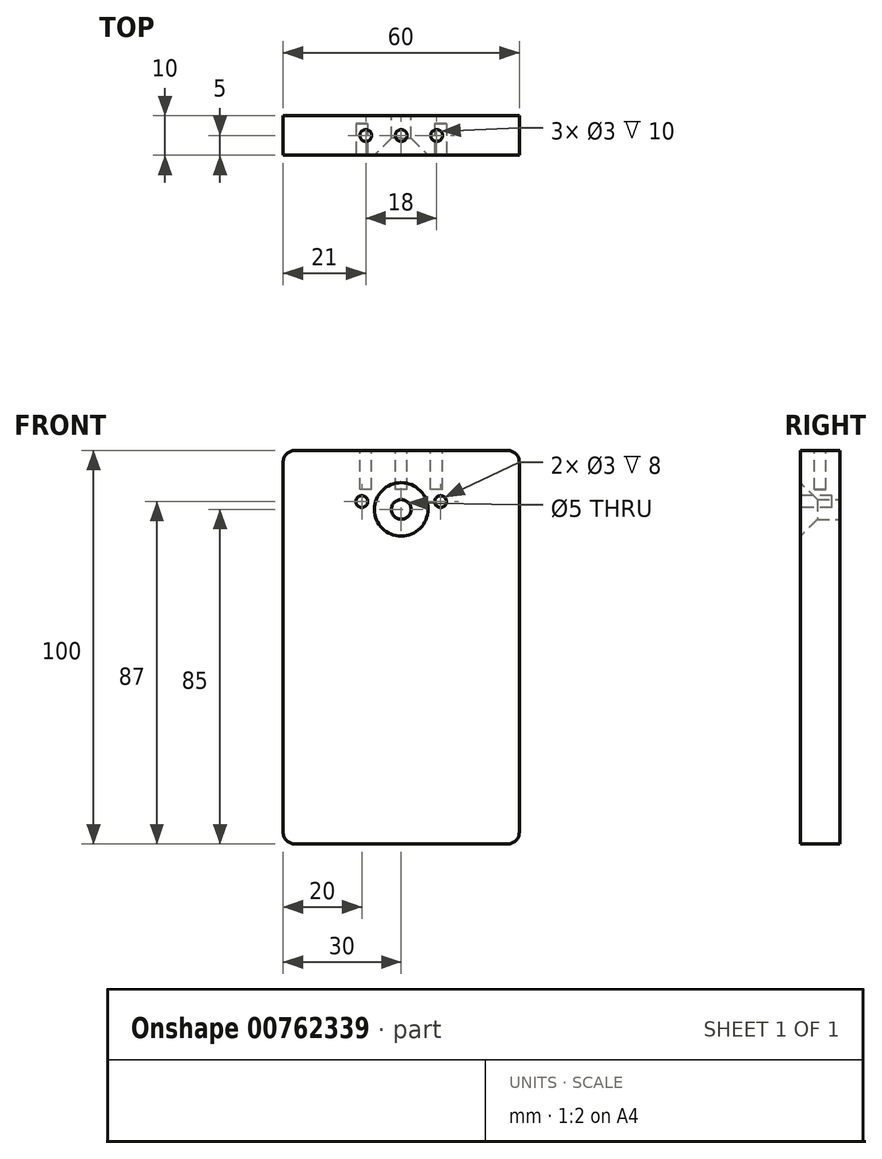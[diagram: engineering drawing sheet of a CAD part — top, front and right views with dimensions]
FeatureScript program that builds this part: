
annotation { "Feature Type Name" : "Feature", "Feature Type Description" : "" }
export const myFeature = defineFeature(function(context is Context, id is Id, definition is map)
    precondition{}
    {
        {
            var Q0;
            Q0=qCreatedBy(makeId("Front.planeOp"),FACE);
            var sketch = newSketch(context, id + "F0", { "sketchPlane" : qUnion([Q0])});
            skLineSegment(sketch, "E0.bottom", {"start": v(30, -50) * mm, "end": v(-30, -50) * mm});
            skLineSegment(sketch, "E0.top", {"start": v(30, 50) * mm, "end": v(-30, 50) * mm});
            skLineSegment(sketch, "E0.left", {"start": v(30, -50) * mm, "end": v(30, 50) * mm});
            skLineSegment(sketch, "E0.right", {"start": v(-30, -50) * mm, "end": v(-30, 50) * mm});
            skPoint(sketch, "E0.middle", {"position": v(0, 0) * mm});
            skSolve(sketch);
        }
        {
            var Q0;
            Q0 = qSketchRegion(id + "F0", true);
            extrude(context, id + "F1", {"entities" : qUnion([Q0]), "depth" : 10 * mm, "offsetDistance" : 25 * mm});
        }
        {
            var Q0;
            Q0=makeQuery(id+"F1.opExtrude","CAP_FACE",FACE,{"disambiguationData":[OSD([sQuery(id+"F0.wireOp",EDGE,"E0.bottom"),sQuery(id+"F0.wireOp",EDGE,"E0.top"),sQuery(id+"F0.wireOp",EDGE,"E0.left"),sQuery(id+"F0.wireOp",EDGE,"E0.right")])],"isStart":false});
            var sketch = newSketch(context, id + "F2", { "sketchPlane" : qUnion([Q0])});
            skCircle(sketch, "E1", {"center": v(10, 37) * mm, "radius": 1.5 * mm});
            skCircle(sketch, "E2", {"center": v(-10, 37) * mm, "radius": 1.5 * mm});
            skSolve(sketch);
        }
        {
            var Q0;
            Q0 = qSketchRegion(id + "F2", true);
            extrude(context, id + "F3", {"entities" : qUnion([Q0]), "operationType" : NewBodyOperationType.REMOVE, "oppositeDirection" : true, "depth" : 8 * mm, "offsetDistance" : 25 * mm});
        }
        {
            var Q0;
            Q0=makeQuery(id+"F1.opExtrude","SWEPT_FACE",FACE,{"disambiguationData":[OSD([sQuery(id+"F0.wireOp",EDGE,"E0.top")])]});
            var sketch = newSketch(context, id + "F4", { "sketchPlane" : qUnion([Q0])});
            skCircle(sketch, "E3", {"center": v(-9, -5) * mm, "radius": 1.5 * mm});
            skCircle(sketch, "E4", {"center": v(9, -5) * mm, "radius": 1.5 * mm});
            skCircle(sketch, "E5", {"center": v(0, -5) * mm, "radius": 1.5 * mm});
            skSolve(sketch);
        }
        {
            var Q0;
            Q0=makeQuery(id+"F4.imprint","IMPRINT",FACE,{"disambiguationData":[TD([[makeQuery(id+"F4.imprint","IMPRINT",EDGE,{"derivedFrom":sQuery(id+"F4.wireOp",EDGE,"E4")}),1.0]])]});
            var Q1;
            Q1=makeQuery(id+"F4.imprint","IMPRINT",FACE,{"disambiguationData":[TD([[makeQuery(id+"F4.imprint","IMPRINT",EDGE,{"derivedFrom":sQuery(id+"F4.wireOp",EDGE,"E5")}),1.0]])]});
            var Q2;
            Q2=makeQuery(id+"F4.imprint","IMPRINT",FACE,{"disambiguationData":[TD([[makeQuery(id+"F4.imprint","IMPRINT",EDGE,{"derivedFrom":sQuery(id+"F4.wireOp",EDGE,"E3")}),1.0]])]});
            extrude(context, id + "F5", {"entities" : qUnion([Q0, Q1, Q2]), "operationType" : NewBodyOperationType.REMOVE, "oppositeDirection" : true, "depth" : 10 * mm, "offsetDistance" : 25 * mm});
        }
        {
            var Q0;
            Q0=makeQuery(id+"F1.opExtrude","CAP_FACE",FACE,{"disambiguationData":[OSD([sQuery(id+"F0.wireOp",EDGE,"E0.bottom"),sQuery(id+"F0.wireOp",EDGE,"E0.top"),sQuery(id+"F0.wireOp",EDGE,"E0.left"),sQuery(id+"F0.wireOp",EDGE,"E0.right")])],"isStart":true});
            var sketch = newSketch(context, id + "F6", { "sketchPlane" : qUnion([Q0])});
            skCircle(sketch, "E6", {"center": v(0, 35) * mm, "radius": 2.5 * mm});
            skSolve(sketch);
        }
        {
            var Q0;
            Q0 = qSketchRegion(id + "F6", true);
            extrude(context, id + "F7", {"entities" : qUnion([Q0]), "operationType" : NewBodyOperationType.REMOVE, "oppositeDirection" : true, "depth" : 25 * mm, "offsetDistance" : 25 * mm});
        }
        {
            var Q0;
            Q0=makeQuery(id+"F7.boolean.opBoolean","INTERSECT",EDGE,{"derivedFrom":[makeQuery(id+"F1.opExtrude","CAP_FACE",FACE,{"disambiguationData":[OSD([sQuery(id+"F0.wireOp",EDGE,"E0.bottom"),sQuery(id+"F0.wireOp",EDGE,"E0.top"),sQuery(id+"F0.wireOp",EDGE,"E0.left"),sQuery(id+"F0.wireOp",EDGE,"E0.right")])],"isStart":false}),makeQuery(id+"F7.opExtrude","SWEPT_FACE",FACE,{"disambiguationData":[OSD([sQuery(id+"F6.wireOp",EDGE,"E6")])]})]});
            chamfer(context, id + "F8", {"entities" : qUnion([Q0]), "width" : 4.3 * mm, "tangentPropagation" : true});
        }
        {
            var Q0;
            Q0=makeQuery(id+"F1.opExtrude","SWEPT_EDGE",EDGE,{"disambiguationData":[OSD([sQuery(id+"F0.wireOp",EDGE,"E0.bottom"),sQuery(id+"F0.wireOp",EDGE,"E0.left")])]});
            var Q1;
            Q1=makeQuery(id+"F1.opExtrude","SWEPT_EDGE",EDGE,{"disambiguationData":[OSD([sQuery(id+"F0.wireOp",EDGE,"E0.bottom"),sQuery(id+"F0.wireOp",EDGE,"E0.right")])]});
            var Q2;
            Q2=makeQuery(id+"F1.opExtrude","SWEPT_EDGE",EDGE,{"disambiguationData":[OSD([sQuery(id+"F0.wireOp",EDGE,"E0.top"),sQuery(id+"F0.wireOp",EDGE,"E0.right")])]});
            var Q3;
            Q3=makeQuery(id+"F1.opExtrude","SWEPT_EDGE",EDGE,{"disambiguationData":[OSD([sQuery(id+"F0.wireOp",EDGE,"E0.top"),sQuery(id+"F0.wireOp",EDGE,"E0.left")])]});
            fillet(context, id + "F9", {"entities" : qUnion([Q0, Q1, Q2, Q3]), "radius" : 3 * mm, "tangentPropagation" : true, "allowEdgeOverflow" : false});
        }
    });
